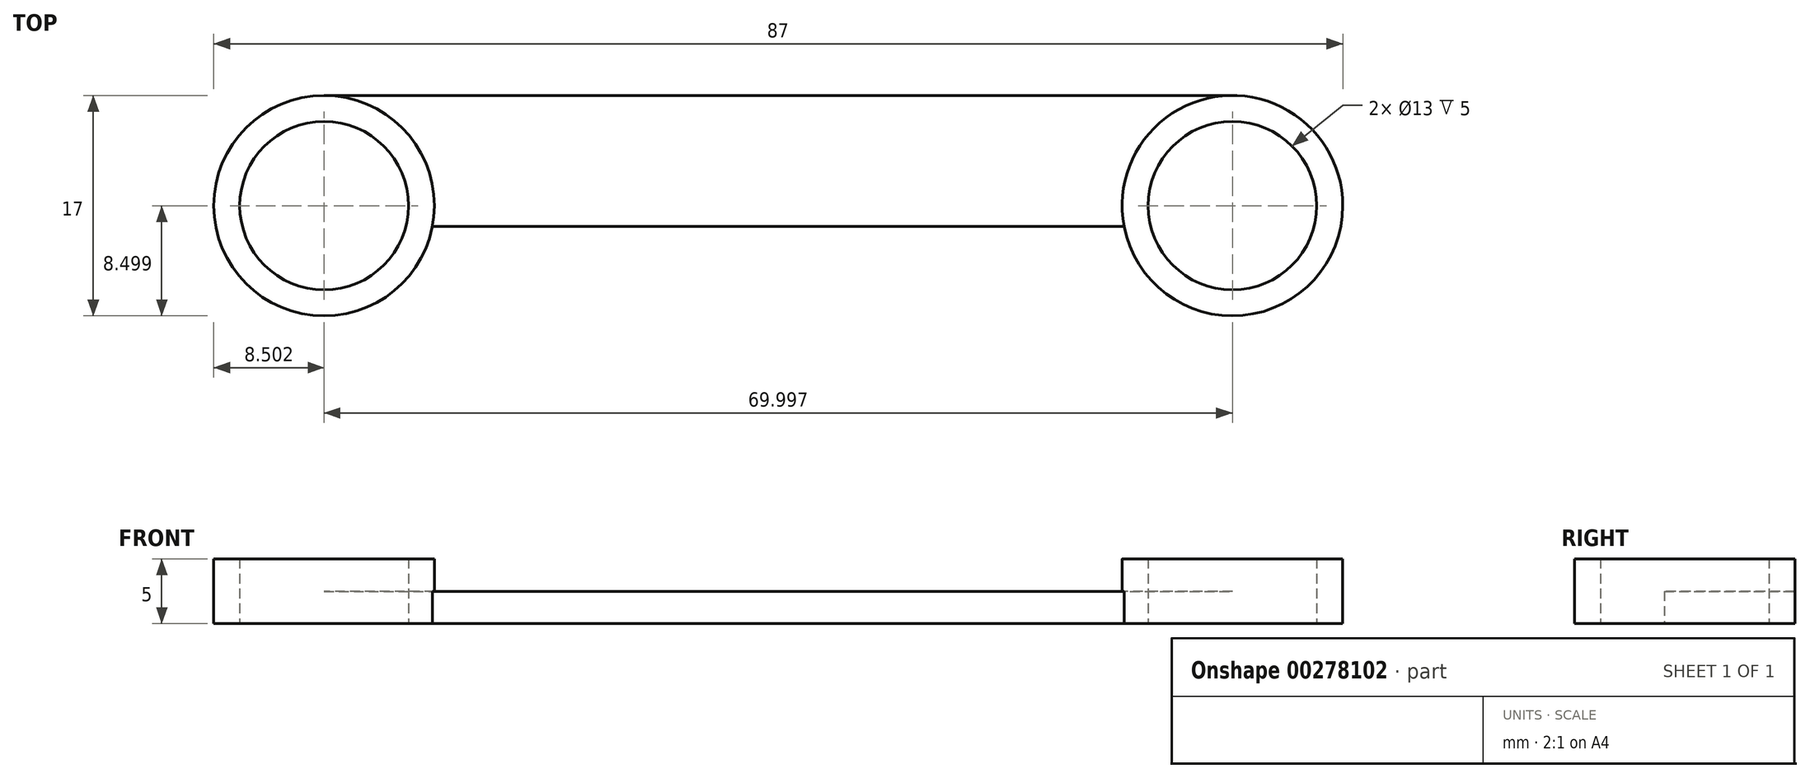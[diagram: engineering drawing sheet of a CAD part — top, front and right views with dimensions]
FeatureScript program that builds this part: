
annotation { "Feature Type Name" : "Feature", "Feature Type Description" : "" }
export const myFeature = defineFeature(function(context is Context, id is Id, definition is map)
    precondition{}
    {
        {
            var Q0;
            Q0=qCreatedBy(makeId("Top.planeOp"),FACE);
            var sketch = newSketch(context, id + "F0", { "sketchPlane" : qUnion([Q0])});
            skCircle(sketch, "E0", {"center": v(-29.65, 3.28) * mm, "radius": 6.5 * mm});
            skCircle(sketch, "E1", {"center": v(-29.65, 3.28) * mm, "radius": 8.5 * mm});
            skCircle(sketch, "E2", {"center": v(40.35, 3.28) * mm, "radius": 6.5 * mm});
            skCircle(sketch, "E3", {"center": v(40.35, 3.28) * mm, "radius": 8.5 * mm});
            skLineSegment(sketch, "E4", {"start": v(-29.65, 11.78) * mm, "end": v(40.35, 11.78) * mm});
            skLineSegment(sketch, "E5", {"start": v(-21.3, 1.69) * mm, "end": v(32, 1.69) * mm});
            skSolve(sketch);
        }
        {
            var Q0;
            {var subQ0=sQuery(id+"F0.wireOp",EDGE,"E4");Q0=makeQuery(id+"F0.imprint","IMPRINT",FACE,{"disambiguationData":[TD([[makeQuery(id+"F0.imprint","IMPRINT",EDGE,{"derivedFrom":subQ0}),-1.0]])]});}
            extrude(context, id + "F1", {"entities" : qUnion([Q0]), "depth" : 2.5 * mm});
        }
        {
            var Q0;
            Q0=makeQuery(id+"F0.imprint","IMPRINT",FACE,{"disambiguationData":[TD([[makeQuery(id+"F0.imprint","IMPRINT",EDGE,{"derivedFrom":sQuery(id+"F0.wireOp",EDGE,"E0")}),-1.0]])]});
            var Q1;
            Q1=makeQuery(id+"F0.imprint","IMPRINT",FACE,{"disambiguationData":[TD([[makeQuery(id+"F0.imprint","IMPRINT",EDGE,{"derivedFrom":sQuery(id+"F0.wireOp",EDGE,"E2")}),-1.0]])]});
            extrude(context, id + "F2", {"entities" : qUnion([Q0, Q1]), "operationType" : NewBodyOperationType.ADD, "depth" : 5 * mm});
        }
    });
